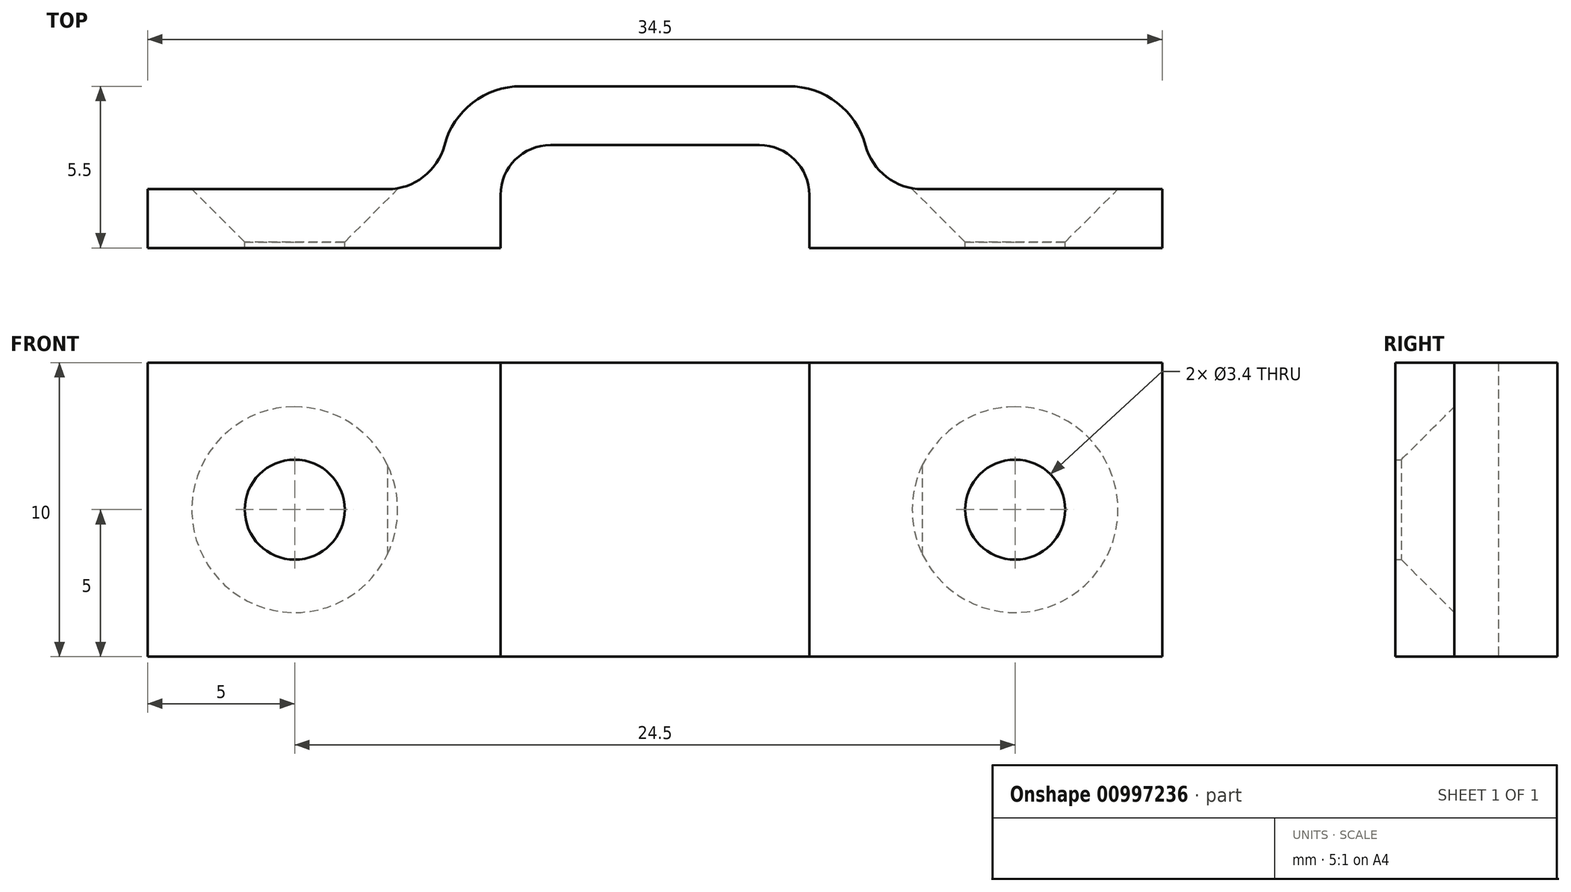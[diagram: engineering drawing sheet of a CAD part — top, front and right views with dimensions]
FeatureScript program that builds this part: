
annotation { "Feature Type Name" : "Feature", "Feature Type Description" : "" }
export const myFeature = defineFeature(function(context is Context, id is Id, definition is map)
    precondition{}
    {
        {
            var Q0;
            Q0=qCreatedBy(makeId("Top.planeOp"),FACE);
            var sketch = newSketch(context, id + "F0", { "sketchPlane" : qUnion([Q0])});
            skLineSegment(sketch, "E0.bottom", {"start": v(-17.25, 1) * mm, "end": v(17.25, 1) * mm});
            skLineSegment(sketch, "E0.top", {"start": v(-17.25, -1) * mm, "end": v(17.25, -1) * mm});
            skLineSegment(sketch, "E0.left", {"start": v(-17.25, 1) * mm, "end": v(-17.25, -1) * mm});
            skLineSegment(sketch, "E0.right", {"start": v(17.25, 1) * mm, "end": v(17.25, -1) * mm});
            skPoint(sketch, "E0.middle", {"position": v(0, 0) * mm});
            skLineSegment(sketch, "E1.bottom", {"start": v(-17.25, 1) * mm, "end": v(-7.25, 1) * mm, "construction": true});
            skLineSegment(sketch, "E1.left", {"start": v(-17.25, 1) * mm, "end": v(-17.25, -1) * mm, "construction": true});
            skLineSegment(sketch, "E1.right", {"start": v(-7.25, 1) * mm, "end": v(-7.25, -1) * mm, "construction": true});
            skLineSegment(sketch, "E2.bottom", {"start": v(17.25, 1) * mm, "end": v(7.25, 1) * mm, "construction": true});
            skLineSegment(sketch, "E2.top", {"start": v(17.25, -1) * mm, "end": v(7.25, -1) * mm, "construction": true});
            skLineSegment(sketch, "E2.left", {"start": v(17.25, 1) * mm, "end": v(17.25, -1) * mm, "construction": true});
            skLineSegment(sketch, "E2.right", {"start": v(7.25, 1) * mm, "end": v(7.25, -1) * mm, "construction": true});
            skPoint(sketch, "E3.oppositeSnap0", {"position": v(7.25, 0) * mm});
            skLineSegment(sketch, "E3.left", {"start": v(-7.25, -1) * mm, "end": v(-7.25, 2.5) * mm, "construction": true});
            skLineSegment(sketch, "E3.right", {"start": v(7.25, -1) * mm, "end": v(7.25, 2.5) * mm, "construction": true});
            skLineSegment(sketch, "E4.bottom", {"start": v(-7.25, -1) * mm, "end": v(-5.25, -1) * mm});
            skLineSegment(sketch, "E4.top", {"start": v(-5.25, 4.5) * mm, "end": v(-4.55, 4.5) * mm});
            skLineSegment(sketch, "E4.left", {"start": v(-7.25, -1) * mm, "end": v(-7.25, 1.8) * mm});
            skLineSegment(sketch, "E4.right", {"start": v(-5.25, -1) * mm, "end": v(-5.25, 0.8) * mm});
            skLineSegment(sketch, "E5.bottom", {"start": v(7.25, -1) * mm, "end": v(5.25, -1) * mm});
            skLineSegment(sketch, "E5.top", {"start": v(5.25, 4.5) * mm, "end": v(4.55, 4.5) * mm});
            skLineSegment(sketch, "E5.left", {"start": v(7.25, -1) * mm, "end": v(7.25, 1.8) * mm});
            skLineSegment(sketch, "E5.right", {"start": v(5.25, -1) * mm, "end": v(5.25, 0.8) * mm});
            skLineSegment(sketch, "E6.bottom", {"start": v(-7.25, 4.5) * mm, "end": v(7.25, 4.5) * mm});
            skLineSegment(sketch, "E6.top", {"start": v(-3.55, 2.5) * mm, "end": v(3.55, 2.5) * mm});
            skLineSegment(sketch, "E6.left", {"start": v(-7.25, 4.5) * mm, "end": v(-7.25, 2.5) * mm});
            skLineSegment(sketch, "E6.right", {"start": v(7.25, 4.5) * mm, "end": v(7.25, 2.5) * mm});
            skArc(sketch, "E7.filletArc", {"start": v(-3.55, 2.5) * mm, "mid": v(-4.75, 2) * mm, "end": v(-5.25, 0.8) * mm});
            skArc(sketch, "E8.filletArc", {"start": v(5.25, 0.8) * mm, "mid": v(4.75, 2) * mm, "end": v(3.55, 2.5) * mm});
            skPoint(sketch, "E9.visualSharp", {"position": v(-7.25, 4.5) * mm});
            skArc(sketch, "E9.filletArc", {"start": v(-4.55, 4.5) * mm, "mid": v(-6.46, 3.7) * mm, "end": v(-7.25, 1.8) * mm});
            skPoint(sketch, "E10.visualSharp", {"position": v(7.25, 4.5) * mm});
            skArc(sketch, "E10.filletArc", {"start": v(7.25, 1.8) * mm, "mid": v(6.46, 3.7) * mm, "end": v(4.55, 4.5) * mm});
            skSolve(sketch);
        }
        {
            var Q0;
            {var subQ0=sQuery(id+"F0.wireOp",EDGE,"E0.left");Q0=makeQuery(id+"F0.imprint","IMPRINT",FACE,{"disambiguationData":[TD([[makeQuery(id+"F0.imprint","IMPRINT",EDGE,{"derivedFrom":subQ0}),1.0]])]});}
            var Q1;
            {var subQ5=sQuery(id+"F0.wireOp",EDGE,"E4.right");Q1=makeQuery(id+"F0.imprint","IMPRINT",FACE,{"disambiguationData":[TD([[makeQuery(id+"F0.imprint","IMPRINT",EDGE,{"derivedFrom":subQ5}),1.0]])]});}
            var Q2;
            {var subQ12=sQuery(id+"F0.wireOp",EDGE,"E6.top");Q2=makeQuery(id+"F0.imprint","IMPRINT",FACE,{"disambiguationData":[TD([[makeQuery(id+"F0.imprint","IMPRINT",EDGE,{"derivedFrom":subQ12}),1.0]])]});}
            var Q3;
            {var subQ0=sQuery(id+"F0.wireOp",EDGE,"E5.right");Q3=makeQuery(id+"F0.imprint","IMPRINT",FACE,{"disambiguationData":[TD([[makeQuery(id+"F0.imprint","IMPRINT",EDGE,{"derivedFrom":subQ0}),-1.0]])]});}
            var Q4;
            {var subQ0=sQuery(id+"F0.wireOp",EDGE,"E0.right");Q4=makeQuery(id+"F0.imprint","IMPRINT",FACE,{"disambiguationData":[TD([[makeQuery(id+"F0.imprint","IMPRINT",EDGE,{"derivedFrom":subQ0}),-1.0]])]});}
            extrude(context, id + "F1", {"entities" : qUnion([Q0, Q1, Q2, Q3, Q4]), "depth" : 10 * mm, "offsetDistance" : 25 * mm});
        }
        {
            var Q0;
            Q0=makeQuery(id+"F1.opExtrude","SWEPT_EDGE",EDGE,{"disambiguationData":[OSD([sQuery(id+"F0.wireOp",EDGE,"E0.bottom"),sQuery(id+"F0.wireOp",EDGE,"E5.left")])]});
            var Q1;
            Q1=makeQuery(id+"F1.opExtrude","SWEPT_EDGE",EDGE,{"disambiguationData":[OSD([sQuery(id+"F0.wireOp",EDGE,"E0.bottom"),sQuery(id+"F0.wireOp",EDGE,"E4.left")])]});
            fillet(context, id + "F2", {"entities" : qUnion([Q0, Q1]), "radius" : 2 * mm, "tangentPropagation" : true, "allowEdgeOverflow" : false});
        }
        {
            var Q0;
            {var subQ0=sQuery(id+"F0.wireOp",EDGE,"E0.bottom");Q0=makeQuery(id+"F1.opExtrude","SWEPT_FACE",FACE,{"disambiguationData":[OSD([subQ0]),TDD([makeQuery(id+"F0.imprint","IMPRINT",EDGE,{"disambiguationData":[TD([[makeQuery(id+"F0.imprint","INTERSECT",VERTEX,{"derivedFrom":[subQ0,sQuery(id+"F0.wireOp",EDGE,"E0.left")]}),-1.0]])],"derivedFrom":subQ0})])]});}
            var sketch = newSketch(context, id + "F3", { "sketchPlane" : qUnion([Q0])});
            skLineSegment(sketch, "E11.bottom", {"start": v(17.25, 0) * mm, "end": v(12.25, 0) * mm, "construction": true});
            skLineSegment(sketch, "E11.top", {"start": v(17.25, 5) * mm, "end": v(12.25, 5) * mm, "construction": true});
            skLineSegment(sketch, "E11.left", {"start": v(17.25, 0) * mm, "end": v(17.25, 5) * mm, "construction": true});
            skLineSegment(sketch, "E11.right", {"start": v(12.25, 0) * mm, "end": v(12.25, 5) * mm, "construction": true});
            skSolve(sketch);
        }
        {
            var Q0;
            Q0=sQuery(id+"F3.wireOp",VERTEX,"E11.top.end");
            var Q1;
            Q1=makeQuery(id+"F1.opExtrude","SWEPT_BODY",BODY,{"disambiguationData":[OSD([sQuery(id+"F0.wireOp",EDGE,"E0.bottom"),sQuery(id+"F0.wireOp",EDGE,"E0.top"),sQuery(id+"F0.wireOp",EDGE,"E0.left"),sQuery(id+"F0.wireOp",EDGE,"E0.right"),sQuery(id+"F0.wireOp",EDGE,"E4.bottom"),sQuery(id+"F0.wireOp",EDGE,"E4.left"),sQuery(id+"F0.wireOp",EDGE,"E4.right"),sQuery(id+"F0.wireOp",EDGE,"E5.bottom"),sQuery(id+"F0.wireOp",EDGE,"E5.left"),sQuery(id+"F0.wireOp",EDGE,"E5.right"),sQuery(id+"F0.wireOp",EDGE,"E6.bottom"),sQuery(id+"F0.wireOp",EDGE,"E6.top"),sQuery(id+"F0.wireOp",EDGE,"E7.filletArc"),sQuery(id+"F0.wireOp",EDGE,"E8.filletArc"),sQuery(id+"F0.wireOp",EDGE,"E9.filletArc"),sQuery(id+"F0.wireOp",EDGE,"E10.filletArc")])]});
            hole(context, id + "F4", {"style" : HoleStyle.C_SINK, "endStyle" : HoleEndStyle.THROUGH, "holeDiameter" : 3.4 * mm, "cSinkDiameter" : 7 * mm, "cSinkAngle" : 90 * degree, "majorDiameter" : 5 * mm, "isTappedThrough" : true, "tappedDepth" : 12 * mm, "tapClearance" : 3, "locations" : qUnion([Q0]), "scope" : qUnion([Q1])});
        }
        {
            var Q0;
            {var subQ0=sQuery(id+"F0.wireOp",EDGE,"E0.bottom");Q0=makeQuery(id+"F1.opExtrude","SWEPT_FACE",FACE,{"disambiguationData":[OSD([subQ0]),TDD([makeQuery(id+"F0.imprint","IMPRINT",EDGE,{"disambiguationData":[TD([[makeQuery(id+"F0.imprint","INTERSECT",VERTEX,{"derivedFrom":[subQ0,sQuery(id+"F0.wireOp",EDGE,"E0.right")]}),1.0]])],"derivedFrom":subQ0})])]});}
            var sketch = newSketch(context, id + "F5", { "sketchPlane" : qUnion([Q0])});
            skLineSegment(sketch, "E12.bottom", {"start": v(-17.25, 10) * mm, "end": v(-12.25, 10) * mm, "construction": true});
            skLineSegment(sketch, "E12.top", {"start": v(-17.25, 5) * mm, "end": v(-12.25, 5) * mm, "construction": true});
            skLineSegment(sketch, "E12.left", {"start": v(-17.25, 10) * mm, "end": v(-17.25, 5) * mm, "construction": true});
            skLineSegment(sketch, "E12.right", {"start": v(-12.25, 10) * mm, "end": v(-12.25, 5) * mm, "construction": true});
            skSolve(sketch);
        }
        {
            var Q0;
            Q0=sQuery(id+"F5.wireOp",VERTEX,"E12.top.end");
            var Q1;
            Q1=makeQuery(id+"F1.opExtrude","SWEPT_BODY",BODY,{"disambiguationData":[OSD([sQuery(id+"F0.wireOp",EDGE,"E0.bottom"),sQuery(id+"F0.wireOp",EDGE,"E0.top"),sQuery(id+"F0.wireOp",EDGE,"E0.left"),sQuery(id+"F0.wireOp",EDGE,"E0.right"),sQuery(id+"F0.wireOp",EDGE,"E4.bottom"),sQuery(id+"F0.wireOp",EDGE,"E4.left"),sQuery(id+"F0.wireOp",EDGE,"E4.right"),sQuery(id+"F0.wireOp",EDGE,"E5.bottom"),sQuery(id+"F0.wireOp",EDGE,"E5.left"),sQuery(id+"F0.wireOp",EDGE,"E5.right"),sQuery(id+"F0.wireOp",EDGE,"E6.bottom"),sQuery(id+"F0.wireOp",EDGE,"E6.top"),sQuery(id+"F0.wireOp",EDGE,"E7.filletArc"),sQuery(id+"F0.wireOp",EDGE,"E8.filletArc"),sQuery(id+"F0.wireOp",EDGE,"E9.filletArc"),sQuery(id+"F0.wireOp",EDGE,"E10.filletArc")])]});
            hole(context, id + "F6", {"style" : HoleStyle.C_SINK, "endStyle" : HoleEndStyle.THROUGH, "holeDiameter" : 3.4 * mm, "cSinkDiameter" : 7 * mm, "cSinkAngle" : 90 * degree, "majorDiameter" : 5 * mm, "isTappedThrough" : true, "tappedDepth" : 12 * mm, "tapClearance" : 3, "locations" : qUnion([Q0]), "scope" : qUnion([Q1])});
        }
    });
